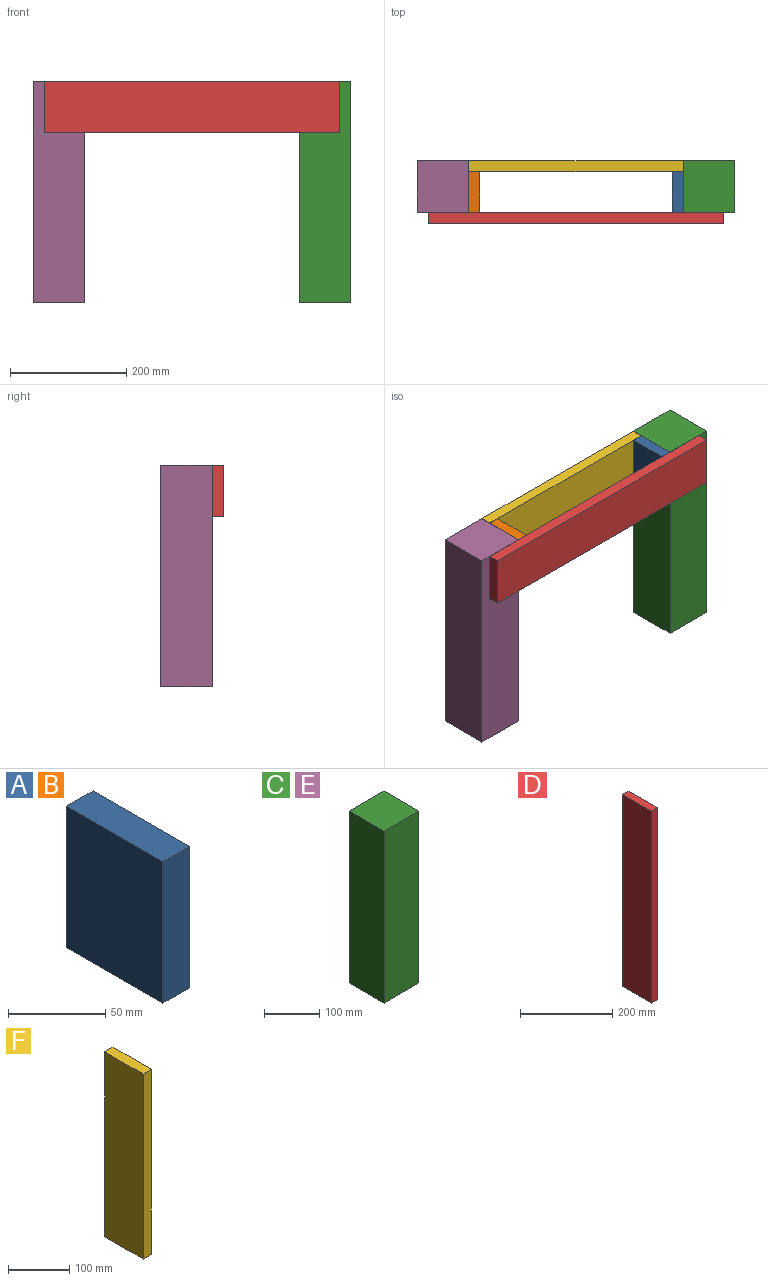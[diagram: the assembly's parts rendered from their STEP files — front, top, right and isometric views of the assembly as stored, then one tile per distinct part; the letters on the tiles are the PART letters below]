
ASSEMBLY  parts=6 mates=5
PART A: 6 faces, bbox 19.1x69.9x88.9 mm
  f0: plane 88.9x19.05mm, normal (0,1,0), area 1693.5mm2, adj f1,f3,f4,f5
  f1: plane 88.9x69.85mm, normal (-1,0,0), area 6209.7mm2, adj f0,f2,f4,f5
  f2: plane 88.9x19.05mm, normal (0,-1,0), area 1693.5mm2, adj f1,f3,f4,f5
  f3: plane 88.9x69.85mm, normal (1,0,0), area 6209.7mm2, adj f0,f2,f4,f5
  f4: plane 69.85x19.05mm, normal (0,0,1), area 1330.6mm2, adj f0,f1,f2,f3
  f5: plane 69.85x19.05mm, normal (0,0,-1), area 1330.6mm2, adj f0,f1,f2,f3
PART B: same geometry as A
PART C: 6 faces, bbox 88.9x88.9x381 mm
  f0: plane 381x88.9mm, normal (0,1,0), area 33870.9mm2, adj f1,f3,f4,f5
  f1: plane 381x88.9mm, normal (-1,0,0), area 33870.9mm2, adj f0,f2,f4,f5
  f2: plane 381x88.9mm, normal (0,-1,0), area 33870.9mm2, adj f1,f3,f4,f5
  f3: plane 381x88.9mm, normal (1,0,0), area 33870.9mm2, adj f0,f2,f4,f5
  f4: plane 88.9x88.9mm, normal (0,0,1), area 7903.2mm2, adj f0,f1,f2,f3
  f5: plane 88.9x88.9mm, normal (0,0,-1), area 7903.2mm2, adj f0,f1,f2,f3
PART D: 6 faces, bbox 19.1x88.9x508 mm
  f0: plane 508x19.05mm, normal (0,1,0), area 9677.4mm2, adj f1,f3,f4,f5
  f1: plane 508x88.9mm, normal (-1,0,0), area 45161.2mm2, adj f0,f2,f4,f5
  f2: plane 508x19.05mm, normal (0,-1,0), area 9677.4mm2, adj f1,f3,f4,f5
  f3: plane 508x88.9mm, normal (1,0,0), area 45161.2mm2, adj f0,f2,f4,f5
  f4: plane 88.9x19.05mm, normal (0,0,1), area 1693.5mm2, adj f0,f1,f2,f3
  f5: plane 88.9x19.05mm, normal (0,0,-1), area 1693.5mm2, adj f0,f1,f2,f3
PART E: same geometry as C
PART F: 6 faces, bbox 19.1x88.9x368.3 mm
  f0: plane 368.3x19.05mm, normal (0,1,0), area 7016.1mm2, adj f1,f3,f4,f5
  f1: plane 368.3x88.9mm, normal (-1,0,0), area 32741.9mm2, adj f0,f2,f4,f5
  f2: plane 368.3x19.05mm, normal (0,-1,0), area 7016.1mm2, adj f1,f3,f4,f5
  f3: plane 368.3x88.9mm, normal (1,0,0), area 32741.9mm2, adj f0,f2,f4,f5
  f4: plane 88.9x19.05mm, normal (0,0,1), area 1693.5mm2, adj f0,f1,f2,f3
  f5: plane 88.9x19.05mm, normal (0,0,-1), area 1693.5mm2, adj f0,f1,f2,f3
PLACE A t=(250.58,-14.69,245.83)mm
PLACE B rot(axis=(0,0,1),180deg) t=(-98.67,4.36,245.83)mm
PLACE C t=(304.55,4.36,-46.27)mm
PLACE D rot(axis=(-0.58,-0.58,0.58),120deg) t=(329.95,-49.62,290.28)mm
PLACE E t=(-152.65,4.36,-46.27)mm
PLACE F rot(axis=(0.58,-0.58,-0.58),120deg) t=(260.1,39.28,290.28)mm
MATE fastened D.f3 <-> C.f2  axis (0,1,0) through (329.95,-40.09,334.73)mm
MATE fastened D.f3 <-> E.f2  axis (0,1,0) through (-178.05,-40.09,290.28)mm
MATE fastened F.f3 <-> B.f2  axis (0,-1,0) through (-108.2,29.76,290.28)mm
MATE fastened B.f3 <-> E.f3  axis (-1,0,0) through (-108.2,-5.17,290.28)mm
MATE fastened A.f3 <-> C.f1  axis (1,0,0) through (260.1,-5.17,334.73)mm
